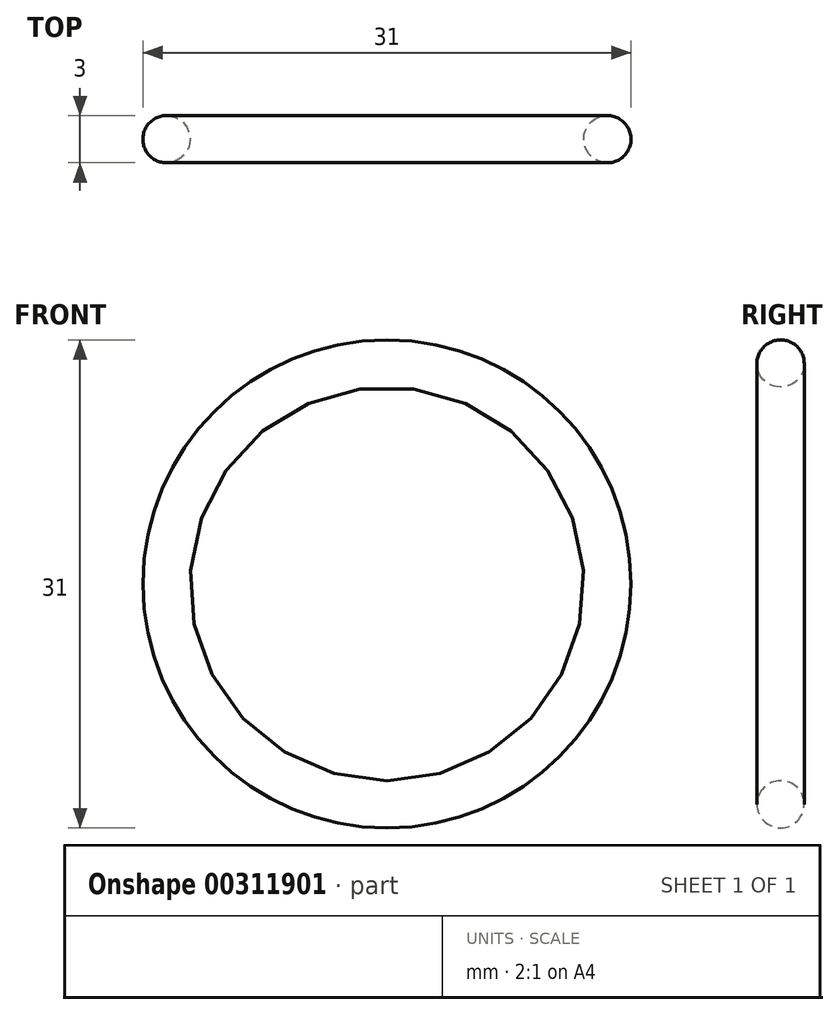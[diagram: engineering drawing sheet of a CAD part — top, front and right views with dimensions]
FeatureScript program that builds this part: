
annotation { "Feature Type Name" : "Feature", "Feature Type Description" : "" }
export const myFeature = defineFeature(function(context is Context, id is Id, definition is map)
    precondition{}
    {
        {
            var Q0;
            Q0=qCreatedBy(makeId("Front.planeOp"),FACE);
            var sketch = newSketch(context, id + "F0", { "sketchPlane" : qUnion([Q0])});
            skCircle(sketch, "E0", {"center": v(-45.9, 28.16) * mm, "radius": 12.5 * mm});
            skCircle(sketch, "E1", {"center": v(-45.9, 28.16) * mm, "radius": 15.5 * mm});
            skSolve(sketch);
        }
        {
            var Q0;
            Q0=makeQuery(id+"F0.imprint","IMPRINT",FACE,{"disambiguationData":[TD([[makeQuery(id+"F0.imprint","IMPRINT",EDGE,{"derivedFrom":sQuery(id+"F0.wireOp",EDGE,"E0")}),-1.0]])]});
            extrude(context, id + "F1", {"entities" : qUnion([Q0]), "depth" : 3 * mm});
        }
        {
            var Q0;
            Q0=makeQuery(id+"F1.opExtrude","CAP_FACE",FACE,{"disambiguationData":[OSD([sQuery(id+"F0.wireOp",EDGE,"E0"),sQuery(id+"F0.wireOp",EDGE,"E1")])],"isStart":false});
            var Q1;
            Q1=makeQuery(id+"F1.opExtrude","CAP_FACE",FACE,{"disambiguationData":[OSD([sQuery(id+"F0.wireOp",EDGE,"E0"),sQuery(id+"F0.wireOp",EDGE,"E1")])],"isStart":true});
            fillet(context, id + "F2", {"entities" : qUnion([Q0, Q1]), "radius" : 1.5 * mm, "tangentPropagation" : true, "allowEdgeOverflow" : false});
        }
    });
